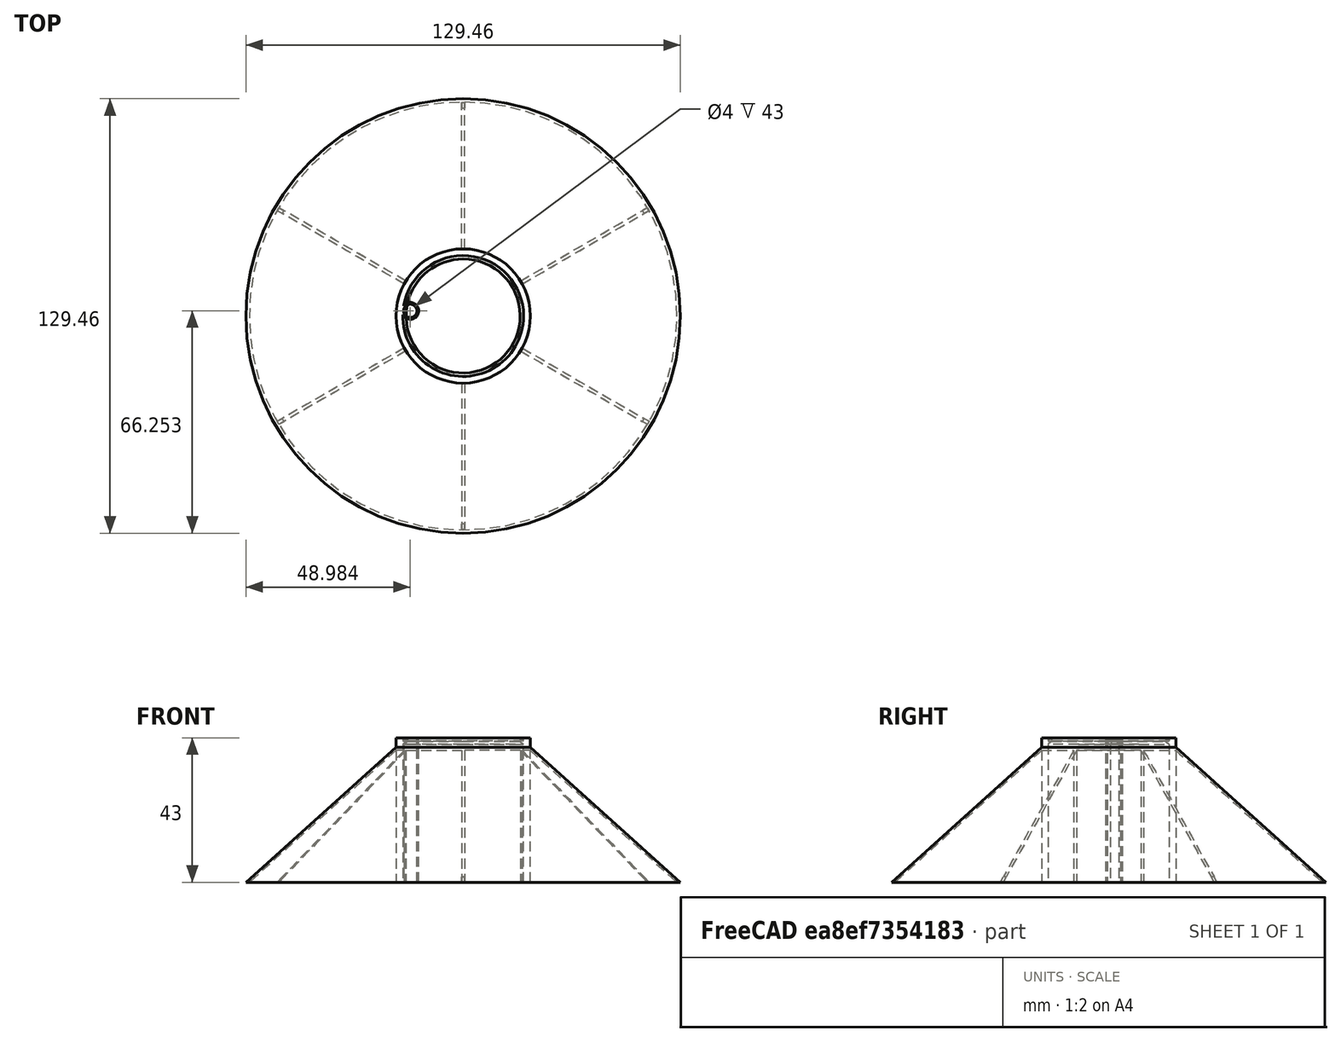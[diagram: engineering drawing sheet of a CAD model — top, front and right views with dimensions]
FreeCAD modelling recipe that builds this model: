
FCSTD DOCUMENT  (FreeCAD 0.20R29603 (Git))
Label: Ez3D-Mini-SaucerX4
License: All rights reserved
LicenseURL: http://en.wikipedia.org/wiki/All_rights_reserved
objects: Mesh::Feature×4, Sketcher::SketchObject×4, PartDesign::Pad×3, PartDesign::PolarPattern×1, PartDesign::Revolution×1, PartDesign::Body×1
note: 14 computed .brp shape members not serialized (recipe doc carries the construction recipe); baked Part::Feature solids carry a one-line shape summary decoded from their .brp

FEATURE [Mesh::Feature] Ez3D_13mmMotorTubeOnly_Body  label="Ez3D-13mmMotorTubeOnly-Body"
  Placement = pos=(-7.6,-7.6,0) rot=(0,0,1;0rad)
FEATURE [Mesh::Feature] Ez3D_13mmMotorTubeOnly_Body001  label="Ez3D-13mmMotorTubeOnly-Body001"
  Placement = pos=(7.6,-7.6,0) rot=(0,0,1;0rad)
FEATURE [Sketcher::SketchObject] Sketch  label="Center Support Structure"
  FullyConstrained = true
  MapMode = 5
  Support = -> [XY_Plane]
  sketch-geometry (2):
    g0: Circle CenterX=0 CenterY=0 CenterZ=0 NormalX=0 NormalY=0 NormalZ=1 AngleXU=0 Radius=18
    g1: Circle CenterX=0 CenterY=0 CenterZ=0 NormalX=0 NormalY=0 NormalZ=1 AngleXU=0 Radius=20
  constraints (4):
    c: Coincident(g0,g-1)
    c: Coincident(g1,g0)
    c: Diameter(g0) = 36
    c: Diameter(g1) = 40
FEATURE [PartDesign::Pad] Pad
  Direction = (0,0,1)
  Length = 43
  Length2 = 10
  Profile = -> Sketch
  ReferenceAxis = -> Sketch [N_Axis]
  Type = 0
FEATURE [Sketcher::SketchObject] Sketch001  label=""Fins""
  FullyConstrained = false
  MapMode = 5
  Placement = pos=(0,0,0) rot=(0.57735,0.57735,0.57735;2.0944rad)
  Support = -> [YZ_Plane]
  sketch-geometry (3):
    g0: LineSegment StartX=18 StartY=42 StartZ=0 EndX=18 EndY=0 EndZ=0
    g1: LineSegment StartX=18 StartY=0 StartZ=0 EndX=63.6847 EndY=0 EndZ=0
    g2: LineSegment StartX=63.6847 StartY=0 StartZ=0 EndX=18 EndY=42 EndZ=0
  constraints (8):
    c: Vertical(g0)
    c: Coincident(g0,g1)
    c: PointOnObject(g1,g-1)
    c: Horizontal(g1)
    c: Coincident(g1,g2)
    c: Coincident(g2,g0)
    c: DistanceY(g0,g0) = 42
    c: DistanceX(g-1,g0) = 18
FEATURE [PartDesign::Pad] Pad001
  BaseFeature = -> Pad
  Direction = (1,-2e-16,3e-16)
  Length = 1
  Length2 = 10
  Midplane = true
  Profile = -> Sketch001
  ReferenceAxis = -> Sketch001 [N_Axis]
  Type = 0
FEATURE [PartDesign::PolarPattern] PolarPattern
  Angle = 360
  Axis = -> Z_Axis
  BaseFeature = -> Pad001
  Occurrences = 6
  Originals = -> [Pad001]
FEATURE [Sketcher::SketchObject] Sketch002  label="Top"
  FullyConstrained = false
  MapMode = 5
  Placement = pos=(0,0,0) rot=(0.57735,0.57735,0.57735;2.0944rad)
  Support = -> [YZ_Plane]
  sketch-geometry (4):
    g0: LineSegment StartX=17 StartY=42.9655 StartZ=0 EndX=17 EndY=41.9655 EndZ=0
    g1: LineSegment StartX=17 StartY=41.9655 StartZ=0 EndX=63.7265 EndY=0 EndZ=0
    g2: LineSegment StartX=63.7265 StartY=0 StartZ=0 EndX=64.7265 EndY=0 EndZ=0
    g3: LineSegment StartX=64.7265 StartY=0 StartZ=0 EndX=17 EndY=42.9655 EndZ=0
  constraints (10):
    c: Coincident(g0,g1)
    c: PointOnObject(g1,g-1)
    c: Coincident(g1,g2)
    c: PointOnObject(g2,g-1)
    c: Coincident(g2,g3)
    c: Coincident(g3,g0)
    c: DistanceX(g2,g2) = 1
    c: Vertical(g0)
    c: DistanceY(g0,g0) = 1
    c: DistanceX(g-1,g0) = 17
FEATURE [PartDesign::Revolution] Revolution
  Angle = 360
  Axis = (-2e-16,3e-16,1)
  Base = (0,0,0)
  BaseFeature = -> PolarPattern
  Profile = -> Sketch002
  ReferenceAxis = -> Sketch002 [V_Axis]
  Reversed = true
FEATURE [Sketcher::SketchObject] Sketch003  label="Launch Lug"
  FullyConstrained = false
  MapMode = 5
  Support = -> [XY_Plane]
  sketch-geometry (2):
    g0: Circle CenterX=-15.7461 CenterY=1.52268 CenterZ=0 NormalX=0 NormalY=0 NormalZ=1 AngleXU=0 Radius=2.5
    g1: Circle CenterX=-15.7461 CenterY=1.52268 CenterZ=0 NormalX=0 NormalY=0 NormalZ=1 AngleXU=0 Radius=2
  constraints (3):
    c: Coincident(g1,g0)
    c: Diameter(g0) = 5
    c: Diameter(g1) = 4
FEATURE [PartDesign::Pad] Pad002  label="Launch Lug001"
  BaseFeature = -> Revolution
  Direction = (0,0,1)
  Length = 43
  Length2 = 10
  Profile = -> Sketch003
  ReferenceAxis = -> Sketch003 [N_Axis]
  Type = 0
FEATURE [PartDesign::Body] Body
  Group = -> [Sketch,Pad,Sketch001,Pad001,PolarPattern,Sketch002,Revolution,Sketch003,Pad002]
  Origin = -> Origin
  Tip = -> Pad002
FEATURE [Mesh::Feature] Ez3D_13mmMotorTubeOnly_Body002  label="Ez3D-13mmMotorTubeOnly-Body002"
  Placement = pos=(7.6,7.6,0) rot=(0,0,1;0rad)
FEATURE [Mesh::Feature] Ez3D_13mmMotorTubeOnly_Body003  label="Ez3D-13mmMotorTubeOnly-Body003"
  Placement = pos=(-7.5,7.5,0) rot=(0,0,1;0rad)
